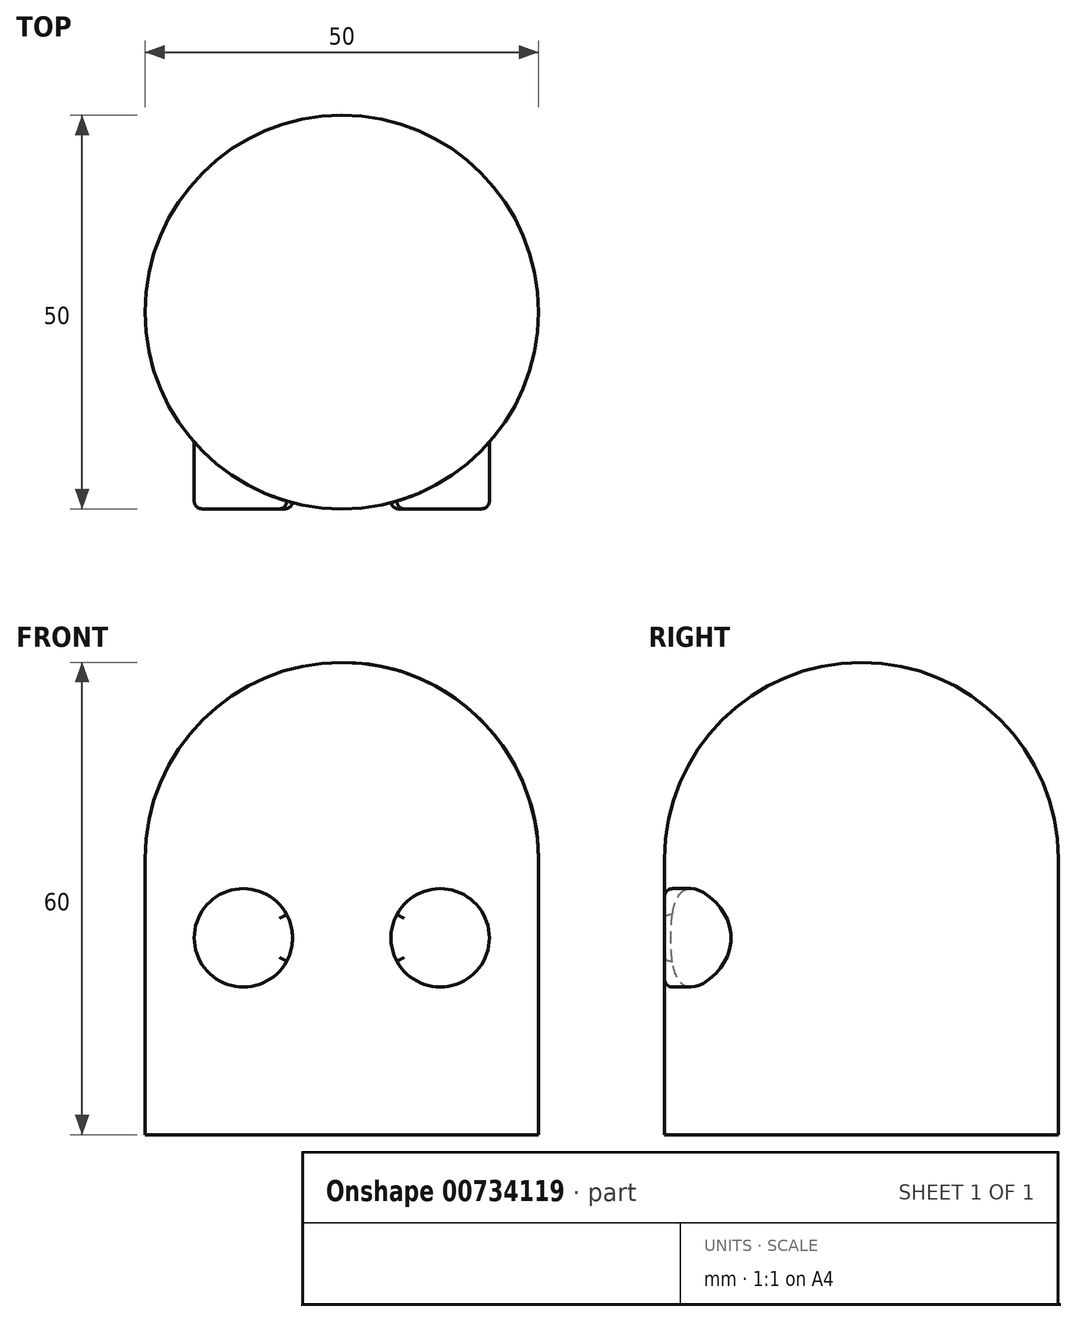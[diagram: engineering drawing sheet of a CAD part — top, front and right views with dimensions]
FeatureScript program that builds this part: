
annotation { "Feature Type Name" : "Feature", "Feature Type Description" : "" }
export const myFeature = defineFeature(function(context is Context, id is Id, definition is map)
    precondition{}
    {
        {
            var Q0;
            Q0=qCreatedBy(makeId("Top.planeOp"),FACE);
            var sketch = newSketch(context, id + "F0", { "sketchPlane" : qUnion([Q0])});
            skCircle(sketch, "E0", {"center": v(0, 0) * mm, "radius": 25 * mm});
            skSolve(sketch);
        }
        {
            var Q0;
            Q0 = qSketchRegion(id + "F0", true);
            extrude(context, id + "F1", {"entities" : qUnion([Q0]), "depth" : 60 * mm, "offsetDistance" : 25 * mm});
        }
        {
            var Q0;
            Q0=makeQuery(id+"F1.opExtrude","CAP_EDGE",EDGE,{"disambiguationData":[OSD([sQuery(id+"F0.wireOp",EDGE,"E0")])],"isStart":false});
            fillet(context, id + "F2", {"entities" : qUnion([Q0]), "radius" : 25 * mm, "tangentPropagation" : true, "allowEdgeOverflow" : false});
        }
        {
            var Q0;
            Q0=qCreatedBy(makeId("Front.planeOp"),FACE);
            var sketch = newSketch(context, id + "F3", { "sketchPlane" : qUnion([Q0])});
            skCircle(sketch, "E1", {"center": v(-12.5, 25) * mm, "radius": 6.25 * mm});
            skSolve(sketch);
        }
        {
            var Q0;
            Q0 = qSketchRegion(id + "F3", true);
            extrude(context, id + "F4", {"entities" : qUnion([Q0]), "operationType" : NewBodyOperationType.ADD, "depth" : 25 * mm, "offsetDistance" : 25 * mm});
        }
        {
            var Q0;
            Q0=makeQuery(id+"F4.opExtrude","CAP_EDGE",EDGE,{"disambiguationData":[OSD([sQuery(id+"F3.wireOp",EDGE,"E1")])],"isStart":false});
            fillet(context, id + "F5", {"entities" : qUnion([Q0]), "radius" : 1 * mm, "tangentPropagation" : true, "allowEdgeOverflow" : false});
        }
        {
            var Q0;
            Q0=makeQuery(id+"F1.opExtrude","SWEPT_BODY",BODY,{"disambiguationData":[OSD([sQuery(id+"F0.wireOp",EDGE,"E0")])]});
            var Q1;
            Q1=qCreatedBy(makeId("Right.planeOp"),FACE);
            mirror(context, id + "F6", {"operationType" : NewBodyOperationType.ADD, "entities" : qUnion([Q0]), "mirrorPlane" : qUnion([Q1])});
        }
    });
